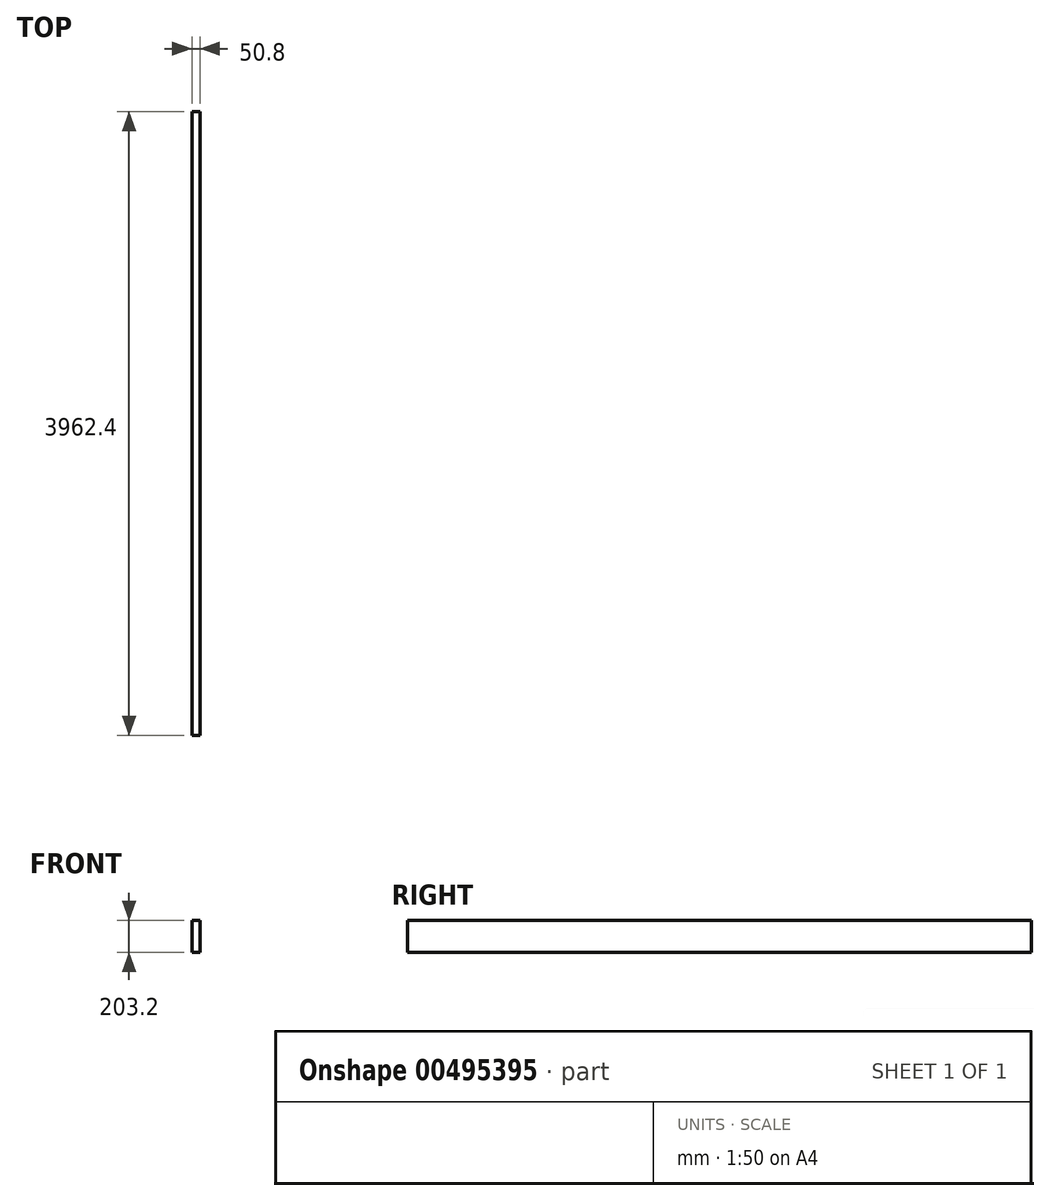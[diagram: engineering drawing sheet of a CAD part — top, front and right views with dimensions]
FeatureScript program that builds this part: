
annotation { "Feature Type Name" : "Feature", "Feature Type Description" : "" }
export const myFeature = defineFeature(function(context is Context, id is Id, definition is map)
    precondition{}
    {
        {
            var Q0;
            Q0=qCreatedBy(makeId("Front.planeOp"),FACE);
            var sketch = newSketch(context, id + "F0", { "sketchPlane" : qUnion([Q0])});
            skLineSegment(sketch, "E0.bottom", {"start": v(0, 0) * mm, "end": v(50.8, 0) * mm});
            skLineSegment(sketch, "E0.top", {"start": v(0, 203.2) * mm, "end": v(50.8, 203.2) * mm});
            skLineSegment(sketch, "E0.left", {"start": v(0, 0) * mm, "end": v(0, 203.2) * mm});
            skLineSegment(sketch, "E0.right", {"start": v(50.8, 0) * mm, "end": v(50.8, 203.2) * mm});
            skSolve(sketch);
        }
        {
            var Q0;
            Q0 = qSketchRegion(id + "F0", true);
            extrude(context, id + "F1", {"entities" : qUnion([Q0]), "depth" : 3962.4 * mm, "offsetDistance" : 25.4 * mm});
        }
    });
